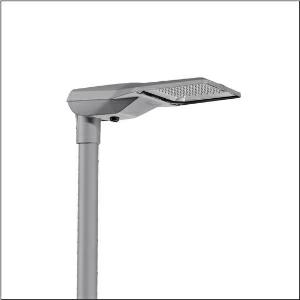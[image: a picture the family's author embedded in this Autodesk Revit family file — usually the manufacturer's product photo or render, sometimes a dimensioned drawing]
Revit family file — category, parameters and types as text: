
# Revit family: streetlight_sl_21_iq_midi___st1_0ab_5xe3m31u08nb_407f
name_source: partatom
category: Lighting Fixtures
units: mm (PartAtom-declared; Revit-internal decimal feet)

## family parameters
Cut with Voids When Loaded = No
Host = Face
Light Source = No
Part Type = Normal
Room Calculation Point = No
Round Connector Dimension = Use Diameter
Shared = No

## types (1)
- --- (1 x LED, 18970 lm, 136.6 W, 3000K)
    Apparent Load = 137 VA
    CIE Flux Codes = 40 74 97 100 100
    Color Rendering = 70
    Color Temperature = 3000K
    Default Elevation = 1800 mm
    Description = Streetlight SL 21 iQ midi, mast luminaire, primary light control with lens, of PMMA, primary optical cover: cover, of toughened safety glass, transparent, light distribution: ST1.0aB, light emission: direct distribution, primary light characteristic: asymmetric, installation type: post-top, side-entry, LED, High Power LED, rated luminous flux: 18.970lm, luminous efficacy: 139lm/W, light colour: 730, colour temperature: 3000K, control: presetting dimming logarithmic, Street-Remote, Auto-Match, Temp-Guard, Lumen-Switch, Night-Set, Smart-Wire, Light-Fading, Desk-Remote (wireless, voltage-free reading and setting of iQ features in the workshop via application-optimized NFC function/RFID function), optimised constant luminous flux control (CLO 2.0), mains connection: 230..240V, AC, 50/60Hz, start of lifetime: 137W, end of service life: 144W, reduction: 61W, luminaire housing, of diecast aluminium, powder-coated, Siteco® metallic grey (DB 702S), corrosivity category C5 mid according to DIN EN ISO 12944, please order mast flange separately, inclination adjustable: 0°, 5°, 10°, 15°, sealing non-destructively replaceable, multi-level sealing system, length: 644mm, width: 335mm, height: 110mm, mast flange for spigot size: 42mm (side-entry): 5XC10008XM4, 60/48mm (side-entry/post-top): 5XC10108XM2, 76/60mm (side-entry/post-top): 5XC10108XM1, Smart Interface below, protection rating (complete): IP66, insulation class (complete): insulation class II (safety insulation), certification: CE, ENEC, ENEC+, VDE, impact resistance: IK09, permissible operating ambient temperature for outdoor applications: -40..+50°C, standard-compliant lighting for roads and squares, packaging unit: 1 piece

Light Distribution: ST1.0aB
    Height = 111 mm
    Lamp = 1 x LED
    Lamp Light Flux = 18970 lm
    Lamp Power = 136.6 W
    Lamp count = 1
    Length = 644 mm
    Luminous efficacy = 139 lm/W
    Manufacturer = Siteco
    ModVariant = No
    Model = 5XE3M31U08NB
    Number of Poles = 1
    OnlyDefault = Yes
    Power Factor = 1
    Product Name = Streetlight SL 21 iQ midi | ST1.0aB
    Product group = mast luminaire | pylon top
    ProductGroupID = 6100
    Protection Class = Protection class II
    Protection Degree = IP 66
    RLX_Detail_Level = 1
    RLX_Emergency_Light_Flux = 0 lm
    RLX_Emergency_Type = 0
    RLX_Emergency_Type_DB = No
    RlxData = <blob elided: 91101 chars, md5=7cf4900b>
    Socket = socket
    Standby Power = 0 W
    System Light Flux = 18970 lm
    System Power = 137 W
    Type Comments = factory setting: luminous flux: 100 % | dim-lin: 254 | 733 mA
    Type Image = l_1004300.jpg
    URL = http://relux.com
    VarID = @adj_060375
    Voltage = 0 V
    Weight = 0.00 kg
    Width = 336 mm

## geometry (parser evidence)
native form markers: Blend x4, Sweep x9
no freeform markers — native parametric forms only
